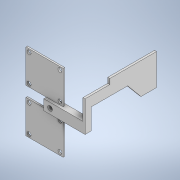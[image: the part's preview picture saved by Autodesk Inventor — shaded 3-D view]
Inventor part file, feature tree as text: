
AUTODESK INVENTOR PART (.ipt)
format: ipt  version: 2020.2 (Build 242310000, 310)  size: 320,000 bytes
history: native  units: mm
features: sketch x14, extrude x11, hole x4, projected_geometry x2
ambient origin geometry x8: Origin, YZ Plane, XZ Plane, XY Plane, X Axis, Y Axis, Z Axis, Center Point
bodies: Body1 (feature_tree), Body2 (feature_tree)
feature tree (31):
  extrude  "Extrusion7"  Depth=6.08mm
  hole  "Hole4"  [1 undecoded]
  sketch  "Sketch16"  dims[d70=12.16mm d71=10.0mm]
  extrude  "Extrusion8"  Depth=10.0mm
  hole  "Hole5"  [1 undecoded]
  extrude  "Extrusion9"  Depth=32.05mm
  extrude  "Extrusion10"  Depth=32.05mm
  extrude  "Extrusion11"  Depth=3.0mm
  hole  "Hole6"  [1 undecoded]
  hole  "Hole7"  [1 undecoded]
  extrude  "Extrusion13"  Depth=26.05mm
  extrude  "Extrusion14"  Depth=4.0mm TaperAngle=0.0deg
  extrude  "Extrusion15"  Depth=10.0mm
  extrude  "Extrusion17"  Depth=2.0mm
  extrude  "Extrusion18"  TaperAngle=90.0deg  [1 undecoded]
  extrude  "Extrusion19"  Depth=45.0mm
  sketch  "Sketch14"  dims[d66=6.08mm d67=6.08mm]
  sketch  "Sketch15"  dims[d68=5.0mm d69=90.0deg]
  sketch  "Sketch17"  dims[d72=2.0mm d73=0.0mm]
  projected_geometry  "Projected Loop2"
  sketch  "Sketch18"  dims[d74=4.5mm d75=6.0mm d76=9.4mm d77=2.0mm d78=90.0deg d79=8.0mm d80=20.594885mm d81=10.0mm]
  projected_geometry  "Projected Loop3"
  sketch  "Sketch19"  dims[d82=35.7mm d83=32.05mm]
  sketch  "Sketch21"  dims[d84=35.7mm d85=32.05mm]
  sketch  "Sketch22"  dims[d86=3.0mm d87=3.0mm]
  sketch  "Sketch23"  dims[d88=29.7mm d89=26.05mm]
  sketch  "Sketch24"  dims[d90=3.0mm d91=3.0mm]
  sketch  "Sketch25"  dims[d92=29.7mm d93=26.05mm]
  sketch  "Sketch27"  dims[d94=1.5mm d95=0.0mm]
  sketch  "Sketch28"  dims[d96=3.9mm d97=6.0mm d98=8.2mm d99=2.0mm d100=90.0deg d101=8.0mm d102=20.594885mm d103=4.0mm d104=0.0mm]
  sketch  "Sketch29"  dims[d105=35.0mm d106=0.0mm d107=10.0mm d108=50.0mm d109=90.0deg d110=45.0mm d111=90.0deg d112=25.0mm d113=2.5mm d114=0.0mm d118=14.05mm d119=90.0deg d120=6.713mm d121=90.0deg d122=10.0mm d123=6.0mm d124=8.2mm d125=2.0mm d126=90.0deg d127=8.0mm d128=20.594885mm d129=8.0mm d130=90.0deg d131=17.5mm d132=90.0deg d133=35.0mm d134=4.2mm d135=6.0mm d136=8.2mm d137=2.0mm d138=90.0deg d139=8.0mm d140=20.594885mm d141=9.0mm d142=90.0deg d145=35.0mm d146=0.0mm d147=11.0mm d148=135.0deg d149=20.0mm d150=35.0mm d151=0.0mm d152=20.0mm d153=90.0deg d154=90.0deg d155=11.45mm d156=4.669mm d157=90.0deg d158=8.0mm d159=17.5mm d160=35.0mm d161=4.2mm d162=4.2mm d163=10.0mm d164=2.0mm d165=0.0mm d166=2.0mm d167=0.0mm d168=35.0mm d169=2.0mm d170=10.0mm d171=0.0mm d172=10.0mm d175=10.0mm d176=0.0mm d177=1.0mm d178=5.0mm d179=0.0mm d180=10.0mm d181=35.0mm d182=0.0mm d183=20.0mm d184=22.68928mm d185=15.0mm d186=30.0mm d187=45.0mm d188=180.0deg d189=5.0mm d190=90.0deg d191=2.0mm d192=0.0mm]
note: 5 required parameter values undecoded (feature->parameter linkage not recoverable at this tier; creation-order binding heuristic only, values carry confidence <= 0.55)
